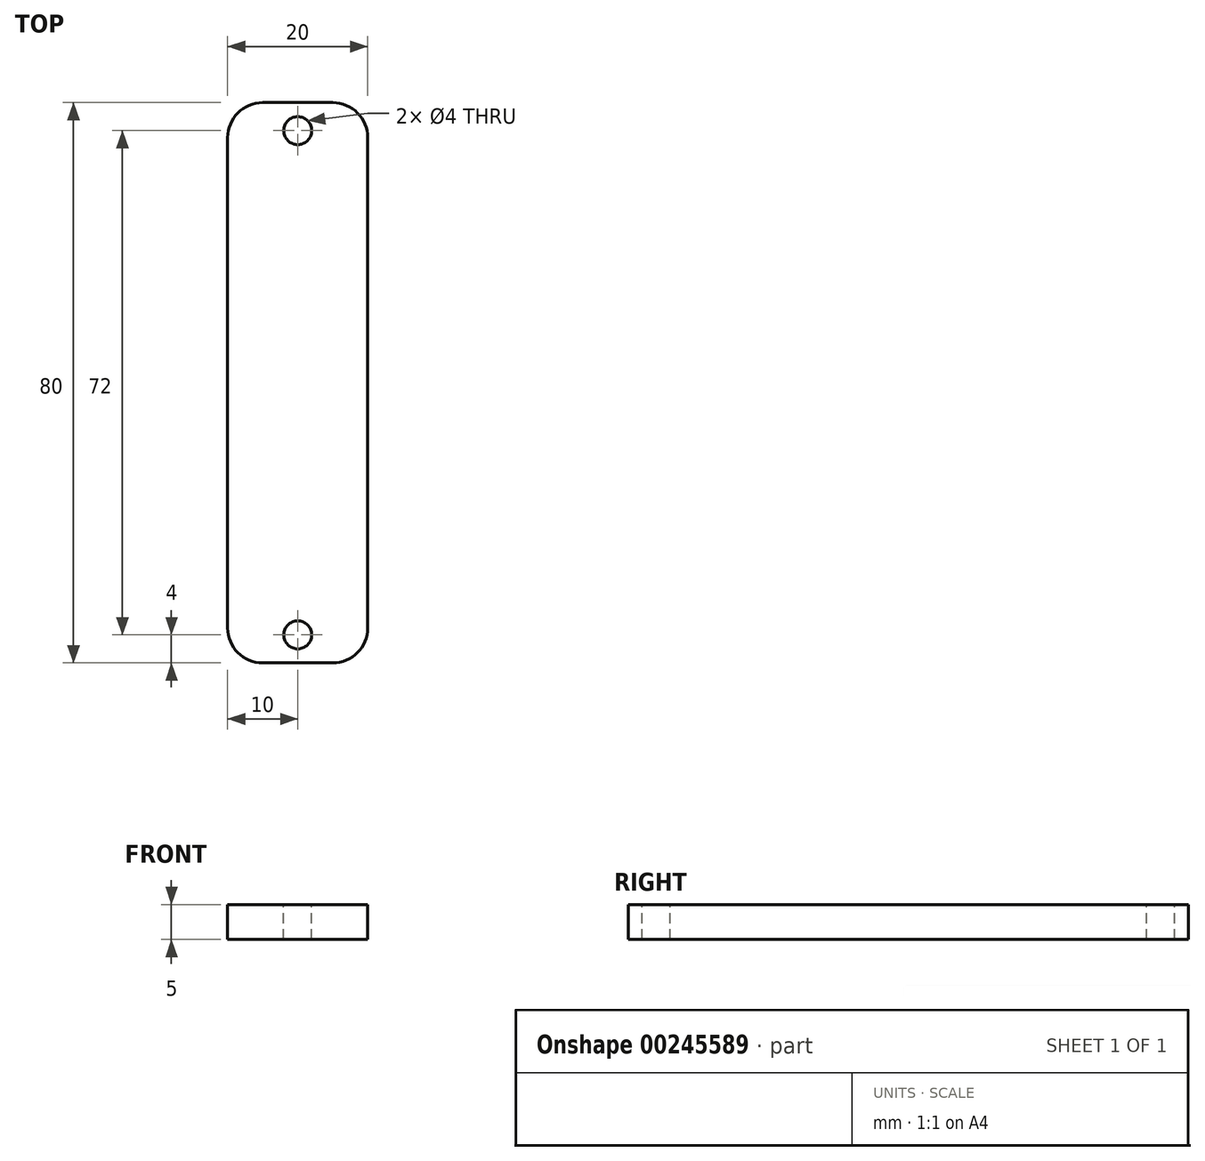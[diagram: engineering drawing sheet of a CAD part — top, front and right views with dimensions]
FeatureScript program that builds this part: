
annotation { "Feature Type Name" : "Feature", "Feature Type Description" : "" }
export const myFeature = defineFeature(function(context is Context, id is Id, definition is map)
    precondition{}
    {
        {
            var Q0;
            Q0=qCreatedBy(makeId("Top.planeOp"),FACE);
            var sketch = newSketch(context, id + "F0", { "sketchPlane" : qUnion([Q0])});
            skLineSegment(sketch, "E0.bottom", {"start": v(10, 40) * mm, "end": v(-10, 40) * mm});
            skLineSegment(sketch, "E0.top", {"start": v(10, -40) * mm, "end": v(-10, -40) * mm});
            skLineSegment(sketch, "E0.left", {"start": v(10, 40) * mm, "end": v(10, -40) * mm});
            skLineSegment(sketch, "E0.right", {"start": v(-10, 40) * mm, "end": v(-10, -40) * mm});
            skPoint(sketch, "E0.middle", {"position": v(0, 0) * mm});
            skSolve(sketch);
        }
        {
            var Q0;
            Q0=makeQuery(id+"F0.imprint","IMPRINT",FACE,{"disambiguationData":[TD([[makeQuery(id+"F0.imprint","IMPRINT",EDGE,{"derivedFrom":sQuery(id+"F0.wireOp",EDGE,"E0.bottom")}),1.0]])]});
            extrude(context, id + "F1", {"entities" : qUnion([Q0]), "depth" : 5 * mm});
        }
        {
            var Q0;
            Q0=makeQuery(id+"F1.opExtrude","CAP_FACE",FACE,{"disambiguationData":[OSD([sQuery(id+"F0.wireOp",EDGE,"E0.bottom"),sQuery(id+"F0.wireOp",EDGE,"E0.top"),sQuery(id+"F0.wireOp",EDGE,"E0.left"),sQuery(id+"F0.wireOp",EDGE,"E0.right")])],"isStart":false});
            var sketch = newSketch(context, id + "F2", { "sketchPlane" : qUnion([Q0])});
            skCircle(sketch, "E1", {"center": v(0, 36) * mm, "radius": 2 * mm});
            skLineSegment(sketch, "E2", {"start": v(-10, 0) * mm, "end": v(10, 0) * mm, "construction": true});
            skCircle(sketch, "E3.MirrorC", {"center": v(0, -36) * mm, "radius": 2 * mm});
            skLineSegment(sketch, "E4", {"start": v(0, 36) * mm, "end": v(0, 40) * mm, "construction": true});
            skSolve(sketch);
        }
        {
            var Q0;
            Q0 = qSketchRegion(id + "F2", true);
            extrude(context, id + "F3", {"entities" : qUnion([Q0]), "operationType" : NewBodyOperationType.REMOVE, "endBound" : BoundingType.THROUGH_ALL, "oppositeDirection" : true, "depth" : 25 * mm});
        }
        {
            var Q0;
            Q0=makeQuery(id+"F1.opExtrude","SWEPT_EDGE",EDGE,{"disambiguationData":[OSD([sQuery(id+"F0.wireOp",EDGE,"E0.top"),sQuery(id+"F0.wireOp",EDGE,"E0.left")])]});
            var Q1;
            Q1=makeQuery(id+"F1.opExtrude","SWEPT_EDGE",EDGE,{"disambiguationData":[OSD([sQuery(id+"F0.wireOp",EDGE,"E0.top"),sQuery(id+"F0.wireOp",EDGE,"E0.right")])]});
            var Q2;
            Q2=makeQuery(id+"F1.opExtrude","SWEPT_EDGE",EDGE,{"disambiguationData":[OSD([sQuery(id+"F0.wireOp",EDGE,"E0.bottom"),sQuery(id+"F0.wireOp",EDGE,"E0.left")])]});
            var Q3;
            Q3=makeQuery(id+"F1.opExtrude","SWEPT_EDGE",EDGE,{"disambiguationData":[OSD([sQuery(id+"F0.wireOp",EDGE,"E0.bottom"),sQuery(id+"F0.wireOp",EDGE,"E0.right")])]});
            fillet(context, id + "F4", {"entities" : qUnion([Q0, Q1, Q2, Q3]), "radius" : 5 * mm, "tangentPropagation" : true, "allowEdgeOverflow" : false});
        }
    });
